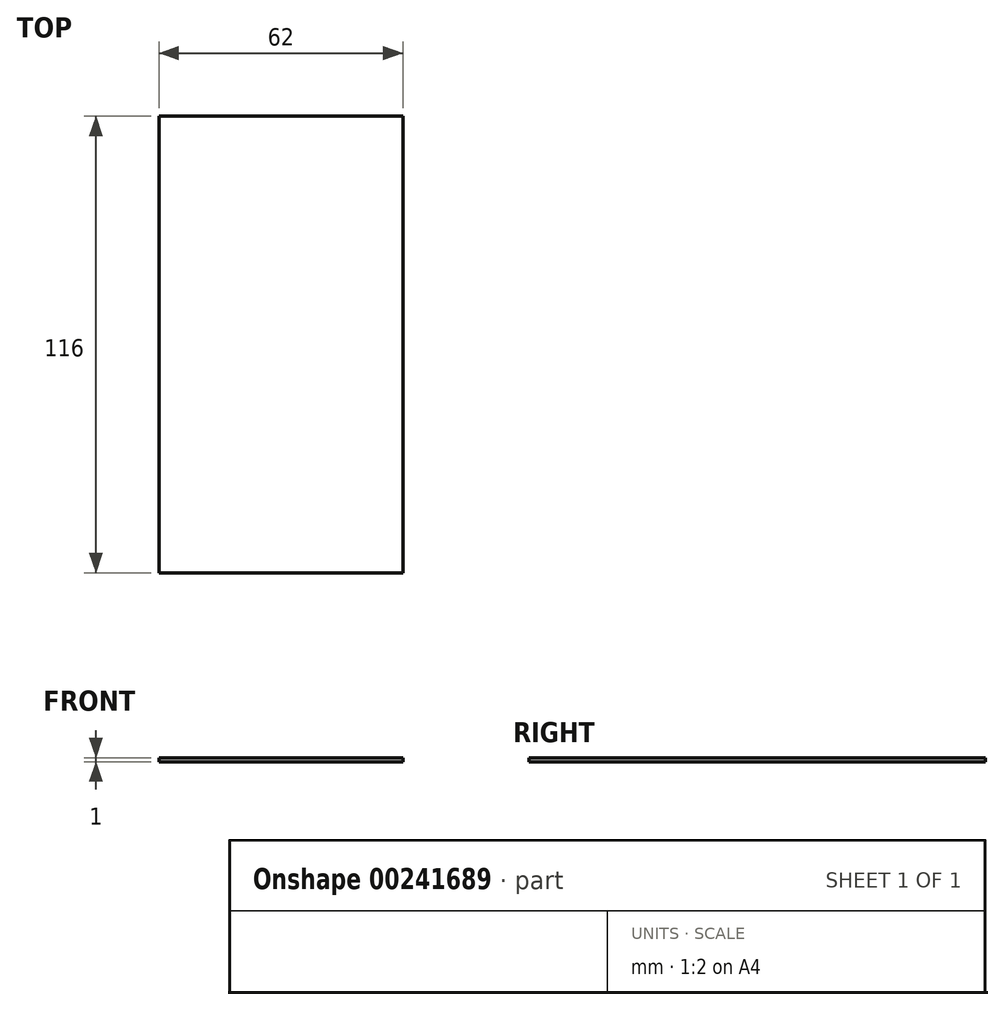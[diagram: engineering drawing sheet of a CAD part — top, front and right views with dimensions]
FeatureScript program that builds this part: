
annotation { "Feature Type Name" : "Feature", "Feature Type Description" : "" }
export const myFeature = defineFeature(function(context is Context, id is Id, definition is map)
    precondition{}
    {
        {
            var Q0;
            Q0=qCreatedBy(makeId("Top.planeOp"),FACE);
            var sketch = newSketch(context, id + "F0", { "sketchPlane" : qUnion([Q0])});
            skLineSegment(sketch, "E0.bottom", {"start": v(31, -58) * mm, "end": v(-31, -58) * mm});
            skLineSegment(sketch, "E0.top", {"start": v(31, 58) * mm, "end": v(-31, 58) * mm});
            skLineSegment(sketch, "E0.left", {"start": v(31, -58) * mm, "end": v(31, 58) * mm});
            skLineSegment(sketch, "E0.right", {"start": v(-31, -58) * mm, "end": v(-31, 58) * mm});
            skPoint(sketch, "E0.middle", {"position": v(0, 0) * mm});
            skSolve(sketch);
        }
        {
            var Q0;
            Q0=makeQuery(id+"F0.imprint","IMPRINT",FACE,{"disambiguationData":[TD([[makeQuery(id+"F0.imprint","IMPRINT",EDGE,{"derivedFrom":sQuery(id+"F0.wireOp",EDGE,"E0.bottom")}),-1.0]])]});
            extrude(context, id + "F1", {"entities" : qUnion([Q0]), "depth" : 1 * mm});
        }
    });
